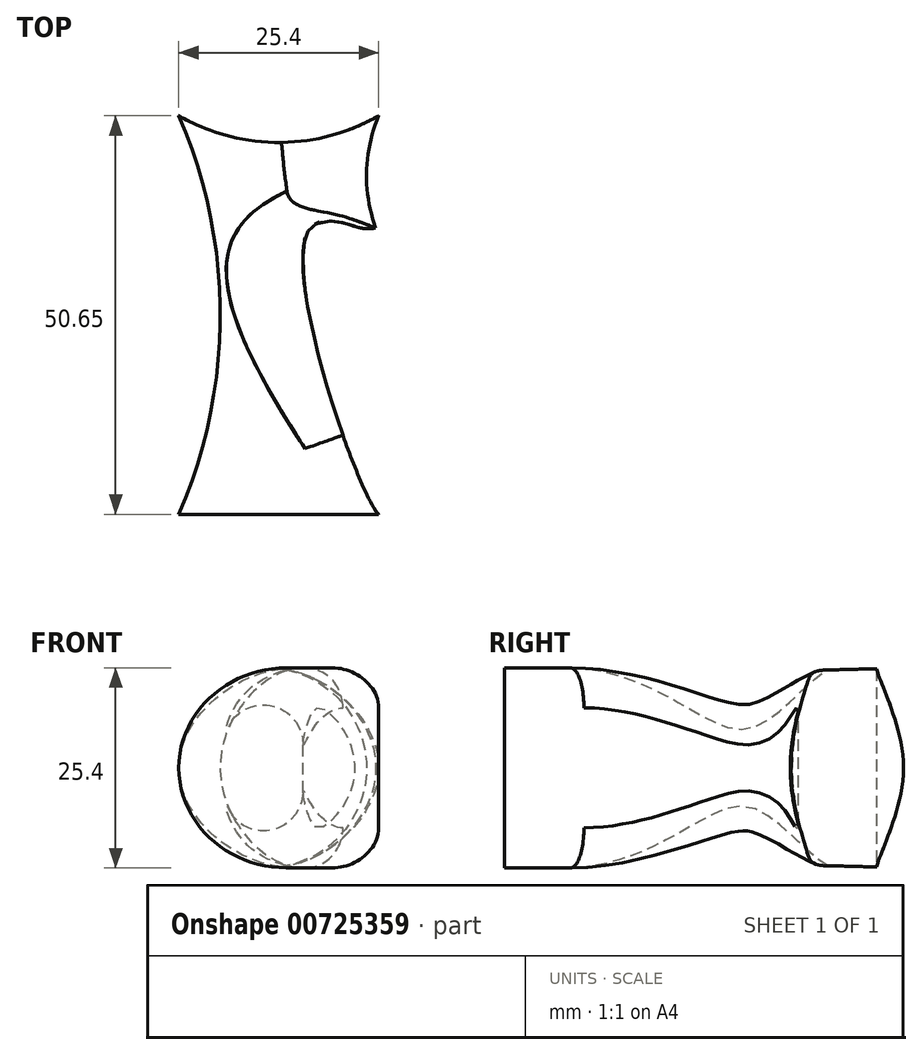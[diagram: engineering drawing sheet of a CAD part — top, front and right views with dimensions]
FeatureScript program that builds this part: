
annotation { "Feature Type Name" : "Feature", "Feature Type Description" : "" }
export const myFeature = defineFeature(function(context is Context, id is Id, definition is map)
    precondition{}
    {
        {
            var Q0;
            Q0=qCreatedBy(makeId("Top.planeOp"),FACE);
            var sketch = newSketch(context, id + "F0", { "sketchPlane" : qUnion([Q0])});
            skLineSegment(sketch, "E0", {"start": v(12.7, 0.15) * mm, "end": v(-12.7, 0.15) * mm});
            skArc(sketch, "E1", {"start": v(-12.7, 0.15) * mm, "mid": v(-7.43, 25.48) * mm, "end": v(-12.7, 50.8) * mm});
            skArc(sketch, "E2", {"start": v(-12.7, 50.8) * mm, "mid": v(0, 47.4) * mm, "end": v(12.7, 50.8) * mm});
            skFitSpline(sketch, "E3", {"points": [v(12.7, 35.56) * mm, v(3.46, 35.56) * mm, v(12.7, 0.15) * mm, v(13.86, 0) * mm], "startDerivative": vector(-40.34, 16.39) * mm, "endDerivative": vector(9.12, 5.42) * mm});
            skArc(sketch, "E4", {"start": v(12.7, 50.8) * mm, "mid": v(11.15, 43.18) * mm, "end": v(12.7, 35.56) * mm});
            skSolve(sketch);
        }
        {
            var Q0;
            Q0 = qSketchRegion(id + "F0", true);
            extrude(context, id + "F1", {"entities" : qUnion([Q0]), "depth" : 25.4 * mm, "offsetDistance" : 25.4 * mm});
        }
        {
            var Q0;
            Q0=makeQuery(id+"F1.opExtrude","CAP_EDGE",EDGE,{"disambiguationData":[OSD([sQuery(id+"F0.wireOp",EDGE,"E4")])],"isStart":true});
            var Q1;
            Q1=makeQuery(id+"F1.opExtrude","CAP_EDGE",EDGE,{"disambiguationData":[OSD([sQuery(id+"F0.wireOp",EDGE,"E4")])],"isStart":false});
            fillet(context, id + "F2", {"entities" : qUnion([Q0, Q1]), "radius" : 12.7 * mm, "tangentPropagation" : true, "allowEdgeOverflow" : false});
        }
        {
            var Q0;
            Q0=makeQuery(id+"F1.opExtrude","CAP_EDGE",EDGE,{"disambiguationData":[OSD([sQuery(id+"F0.wireOp",EDGE,"E1")])],"isStart":true});
            var Q1;
            Q1=makeQuery(id+"F1.opExtrude","CAP_EDGE",EDGE,{"disambiguationData":[OSD([sQuery(id+"F0.wireOp",EDGE,"E1")])],"isStart":false});
            fillet(context, id + "F3", {"entities" : qUnion([Q0, Q1]), "radius" : 12.7 * mm, "tangentPropagation" : true, "allowEdgeOverflow" : false});
        }
        {
            var Q0;
            Q0=makeQuery(id+"F1.opExtrude","CAP_EDGE",EDGE,{"disambiguationData":[OSD([sQuery(id+"F0.wireOp",EDGE,"E3")])],"isStart":true});
            var Q1;
            Q1=makeQuery(id+"F1.opExtrude","CAP_EDGE",EDGE,{"disambiguationData":[OSD([sQuery(id+"F0.wireOp",EDGE,"E3")])],"isStart":false});
            fillet(context, id + "F4", {"entities" : qUnion([Q0, Q1]), "radius" : 5.08 * mm, "tangentPropagation" : true, "allowEdgeOverflow" : false});
        }
        {
            var Q0;
            Q0=makeQuery(id+"F4.opFillet","BLEND_EDGE",EDGE,{"blendedFrom":[makeQuery(id+"F1.opExtrude","CAP_EDGE",EDGE,{"disambiguationData":[OSD([sQuery(id+"F0.wireOp",EDGE,"E3")])],"isStart":true}),makeQuery(id+"F3.opFillet","BLEND_FACE",FACE,{"disambiguationData":[OSD([sQuery(id+"F0.wireOp",EDGE,"E1")])]})],"blendedInto":[makeQuery(id+"F3.opFillet","BLEND_FACE",FACE,{"disambiguationData":[OSD([sQuery(id+"F0.wireOp",EDGE,"E1")])]})]});
            fillet(context, id + "F5", {"entities" : qUnion([Q0]), "radius" : 5.08 * mm, "tangentPropagation" : true, "allowEdgeOverflow" : false});
        }
        {
            var Q0;
            Q0=makeQuery(id+"F4.opFillet","BLEND_EDGE",EDGE,{"blendedFrom":[makeQuery(id+"F1.opExtrude","CAP_EDGE",EDGE,{"disambiguationData":[OSD([sQuery(id+"F0.wireOp",EDGE,"E3")])],"isStart":false}),makeQuery(id+"F3.opFillet","BLEND_FACE",FACE,{"disambiguationData":[OSD([sQuery(id+"F0.wireOp",EDGE,"E1")])]})],"blendedInto":[makeQuery(id+"F3.opFillet","BLEND_FACE",FACE,{"disambiguationData":[OSD([sQuery(id+"F0.wireOp",EDGE,"E1")])]})]});
            fillet(context, id + "F6", {"entities" : qUnion([Q0]), "radius" : 5.08 * mm, "tangentPropagation" : true, "allowEdgeOverflow" : false});
        }
    });
